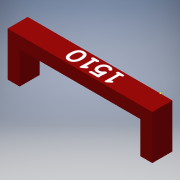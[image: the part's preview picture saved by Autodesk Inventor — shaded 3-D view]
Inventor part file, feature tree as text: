
AUTODESK INVENTOR PART (.ipt)
format: ipt  version: 2016 (Build 200138000, 138)  size: 120,320 bytes
history: native  units: in
note: dims shown in document units (in); Inventor stores cm internally (conversion verified against a paired STEP export)
features: sketch x2, extrude x1, fillet x1
ambient origin geometry x8: Origin, YZ Plane, XZ Plane, XY Plane, X Axis, Y Axis, Z Axis, Center Point
bodies: Solid1 (feature_tree)
feature tree (4):
  extrude  "Extrusion1"  Depth=11.0in
  sketch  "Sketch2"  dims[d3=3.0in d4=3.0in d5=8.0in d6=5.0in d7=0.0in d8=1.0in]
  fillet  "Fillet1"  Radius=33.0in
  sketch  "Sketch1"  dims[d0=3.0in d1=11.0in d2=33.0in]
